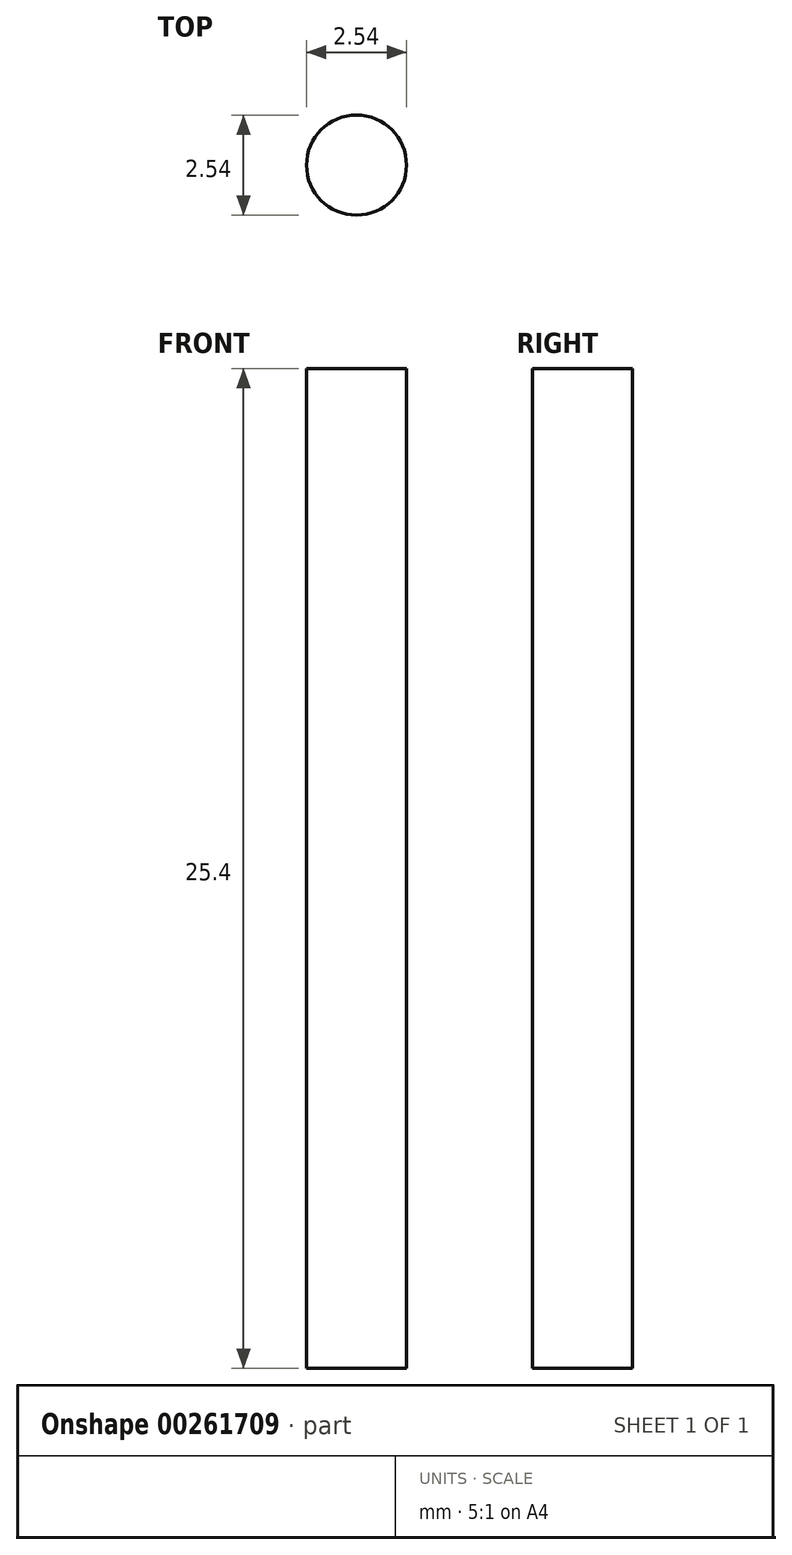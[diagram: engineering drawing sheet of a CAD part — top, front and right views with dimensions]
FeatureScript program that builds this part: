
annotation { "Feature Type Name" : "Feature", "Feature Type Description" : "" }
export const myFeature = defineFeature(function(context is Context, id is Id, definition is map)
    precondition{}
    {
        {
            var Q0;
            Q0=qCreatedBy(makeId("Front.planeOp"),FACE);
            var sketch = newSketch(context, id + "F0", { "sketchPlane" : qUnion([Q0])});
            skLineSegment(sketch, "E0.bottom", {"start": v(-1.27, 12.7) * mm, "end": v(1.27, 12.7) * mm});
            skLineSegment(sketch, "E0.top", {"start": v(-1.27, -12.7) * mm, "end": v(1.27, -12.7) * mm});
            skLineSegment(sketch, "E0.left", {"start": v(-1.27, 12.7) * mm, "end": v(-1.27, -12.7) * mm});
            skLineSegment(sketch, "E0.right", {"start": v(1.27, 12.7) * mm, "end": v(1.27, -12.7) * mm});
            skLineSegment(sketch, "E1", {"start": v(0, 12.7) * mm, "end": v(0, -12.7) * mm});
            skSolve(sketch);
        }
        {
            var Q0;
            {var subQ0=sQuery(id+"F0.wireOp",EDGE,"E0.right");Q0=makeQuery(id+"F0.imprint","IMPRINT",FACE,{"disambiguationData":[TD([[makeQuery(id+"F0.imprint","IMPRINT",EDGE,{"derivedFrom":subQ0}),-1.0]])]});}
            var Q1;
            Q1=sQuery(id+"F0.wireOp",EDGE,"E1");
            revolve(context, id + "F1", {"entities" : qUnion([Q0]), "axis" : qUnion([Q1]), "revolveType" : RevolveType.FULL});
        }
    });
